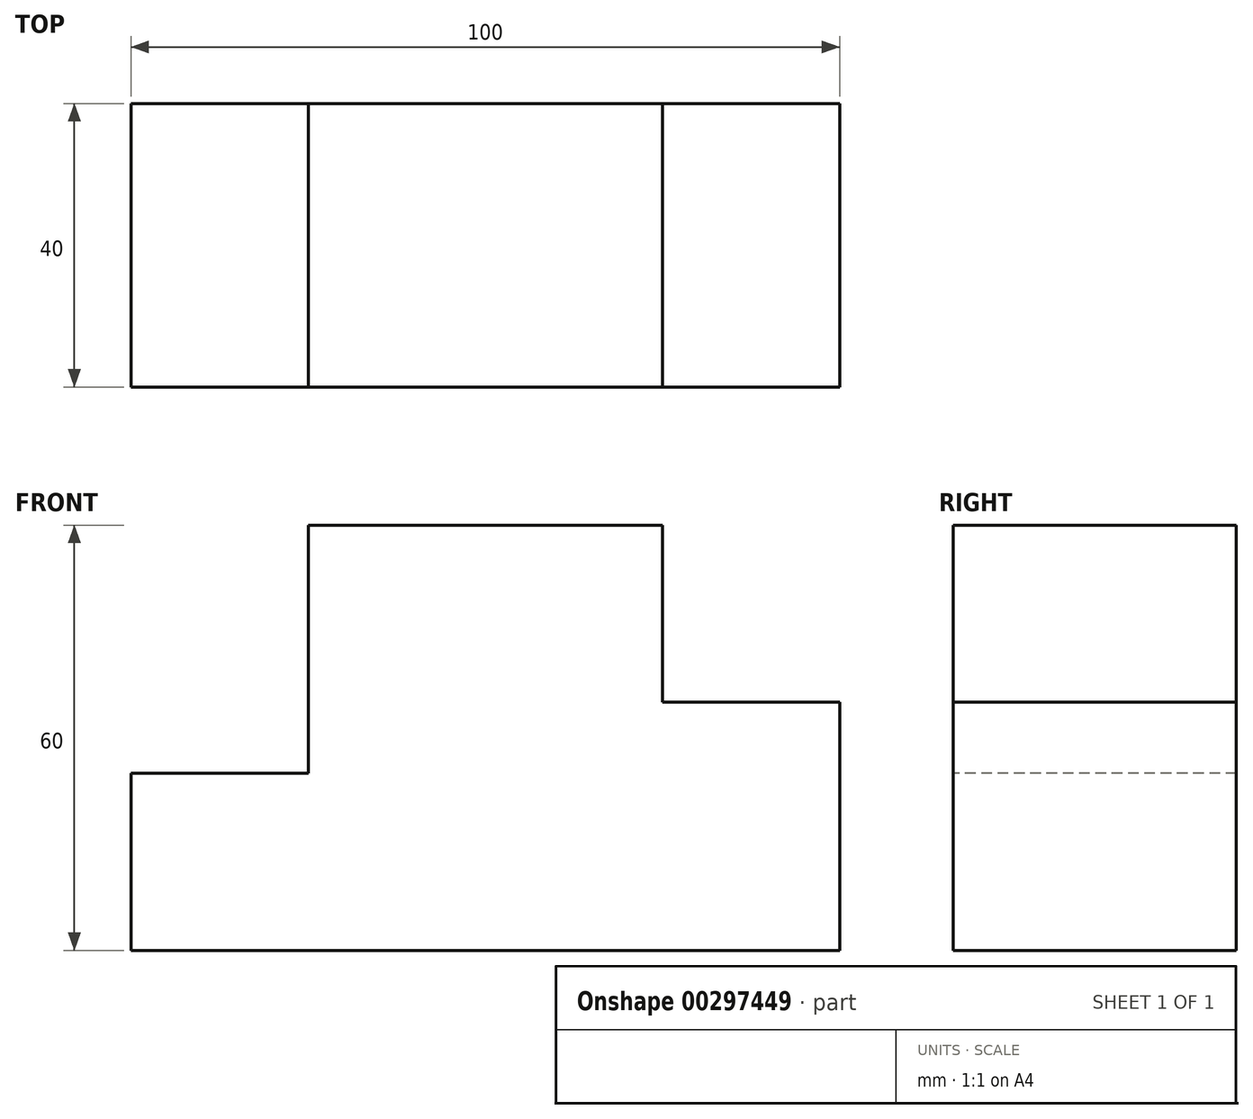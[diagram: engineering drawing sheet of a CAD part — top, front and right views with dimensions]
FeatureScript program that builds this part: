
annotation { "Feature Type Name" : "Feature", "Feature Type Description" : "" }
export const myFeature = defineFeature(function(context is Context, id is Id, definition is map)
    precondition{}
    {
        {
            var Q0;
            Q0=qCreatedBy(makeId("Front.planeOp"),FACE);
            var sketch = newSketch(context, id + "F0", { "sketchPlane" : qUnion([Q0])});
            skLineSegment(sketch, "E0.bottom", {"start": v(-50, -30) * mm, "end": v(50, -30) * mm});
            skLineSegment(sketch, "E0.top", {"start": v(-50, 30) * mm, "end": v(50, 30) * mm});
            skLineSegment(sketch, "E0.left", {"start": v(-50, -30) * mm, "end": v(-50, 30) * mm});
            skLineSegment(sketch, "E0.right", {"start": v(50, -30) * mm, "end": v(50, 30) * mm});
            skPoint(sketch, "E0.middle", {"position": v(0, 0) * mm});
            skSolve(sketch);
        }
        {
            var Q0;
            Q0 = qSketchRegion(id + "F0", true);
            extrude(context, id + "F1", {"entities" : qUnion([Q0]), "depth" : 40 * mm});
        }
        {
            var Q0;
            Q0=makeQuery(id+"F1.opExtrude","CAP_FACE",FACE,{"disambiguationData":[OSD([sQuery(id+"F0.wireOp",EDGE,"E0.bottom"),sQuery(id+"F0.wireOp",EDGE,"E0.top"),sQuery(id+"F0.wireOp",EDGE,"E0.left"),sQuery(id+"F0.wireOp",EDGE,"E0.right")])],"isStart":false});
            var sketch = newSketch(context, id + "F2", { "sketchPlane" : qUnion([Q0])});
            skLineSegment(sketch, "E1.bottom", {"start": v(50, 5) * mm, "end": v(25, 5) * mm});
            skLineSegment(sketch, "E1.top", {"start": v(50, 30) * mm, "end": v(25, 30) * mm});
            skLineSegment(sketch, "E1.left", {"start": v(50, 5) * mm, "end": v(50, 30) * mm});
            skLineSegment(sketch, "E1.right", {"start": v(25, 5) * mm, "end": v(25, 30) * mm});
            skSolve(sketch);
        }
        {
            var Q0;
            Q0 = qSketchRegion(id + "F2", true);
            extrude(context, id + "F3", {"entities" : qUnion([Q0]), "operationType" : NewBodyOperationType.REMOVE, "endBound" : BoundingType.THROUGH_ALL, "oppositeDirection" : true, "depth" : 25 * mm});
        }
        {
            var Q0;
            Q0=makeQuery(id+"F1.opExtrude","CAP_FACE",FACE,{"disambiguationData":[OSD([sQuery(id+"F0.wireOp",EDGE,"E0.bottom"),sQuery(id+"F0.wireOp",EDGE,"E0.top"),sQuery(id+"F0.wireOp",EDGE,"E0.left"),sQuery(id+"F0.wireOp",EDGE,"E0.right")])],"isStart":false});
            var sketch = newSketch(context, id + "F4", { "sketchPlane" : qUnion([Q0])});
            skLineSegment(sketch, "E2.bottom", {"start": v(-25, 30) * mm, "end": v(-50, 30) * mm});
            skLineSegment(sketch, "E2.top", {"start": v(-25, -5) * mm, "end": v(-50, -5) * mm});
            skLineSegment(sketch, "E2.left", {"start": v(-25, 30) * mm, "end": v(-25, -5) * mm});
            skLineSegment(sketch, "E2.right", {"start": v(-50, 30) * mm, "end": v(-50, -5) * mm});
            skSolve(sketch);
        }
        {
            var Q0;
            Q0 = qSketchRegion(id + "F4", true);
            extrude(context, id + "F5", {"entities" : qUnion([Q0]), "operationType" : NewBodyOperationType.REMOVE, "endBound" : BoundingType.THROUGH_ALL, "oppositeDirection" : true, "depth" : 25 * mm});
        }
    });
